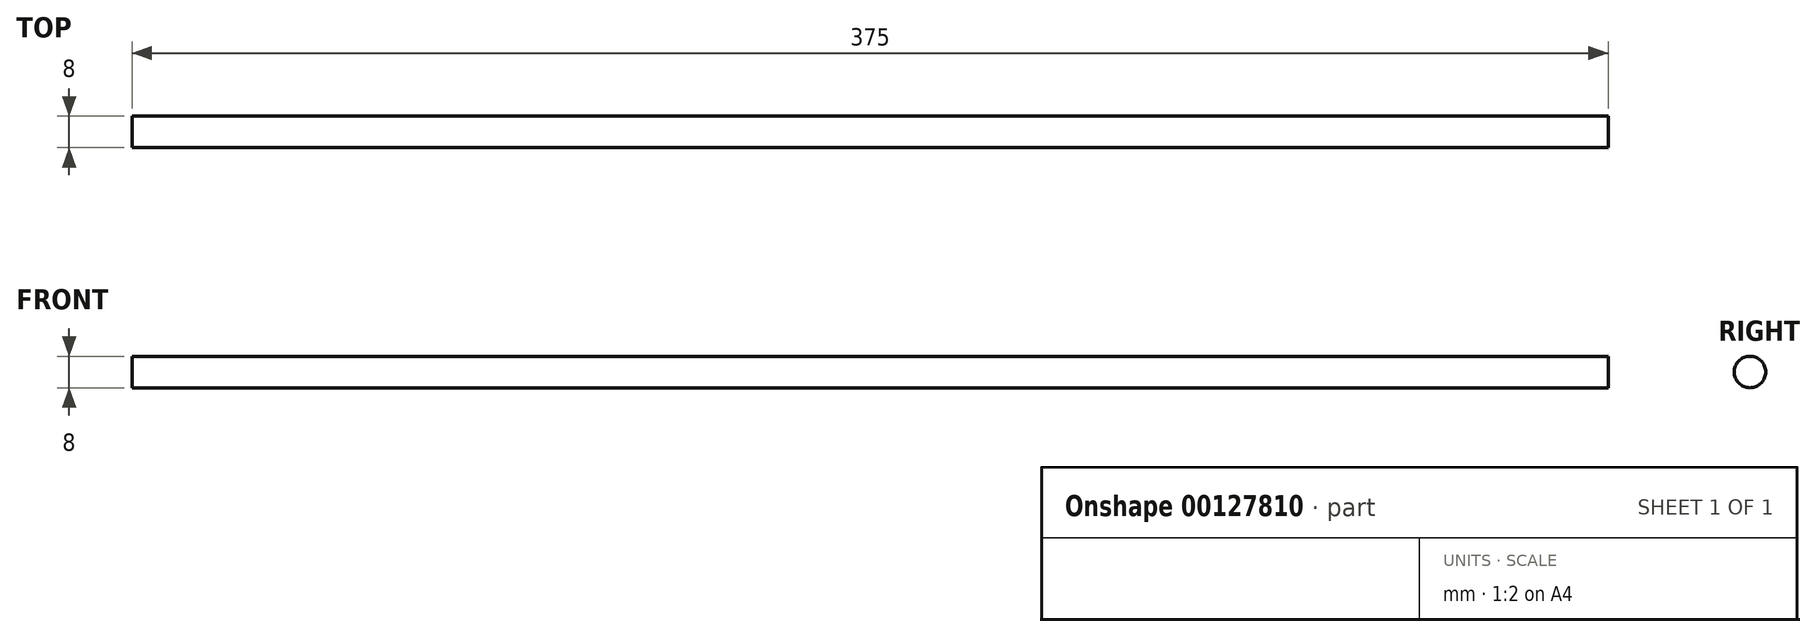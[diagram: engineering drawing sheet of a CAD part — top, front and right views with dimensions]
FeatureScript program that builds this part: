
annotation { "Feature Type Name" : "Feature", "Feature Type Description" : "" }
export const myFeature = defineFeature(function(context is Context, id is Id, definition is map)
    precondition{}
    {
        {
            var Q0;
            Q0=qCreatedBy(makeId("Right.planeOp"),FACE);
            var sketch = newSketch(context, id + "F0", { "sketchPlane" : qUnion([Q0])});
            skCircle(sketch, "E0", {"center": v(0, 0) * mm, "radius": 4 * mm});
            skSolve(sketch);
        }
        {
            var Q0;
            Q0=qSketchRegion(id+"F0",true);
            extrude(context, id + "F1", {"entities" : qUnion([Q0]), "endBound" : BoundingType.SYMMETRIC, "depth" : 375 * mm});
        }
    });
